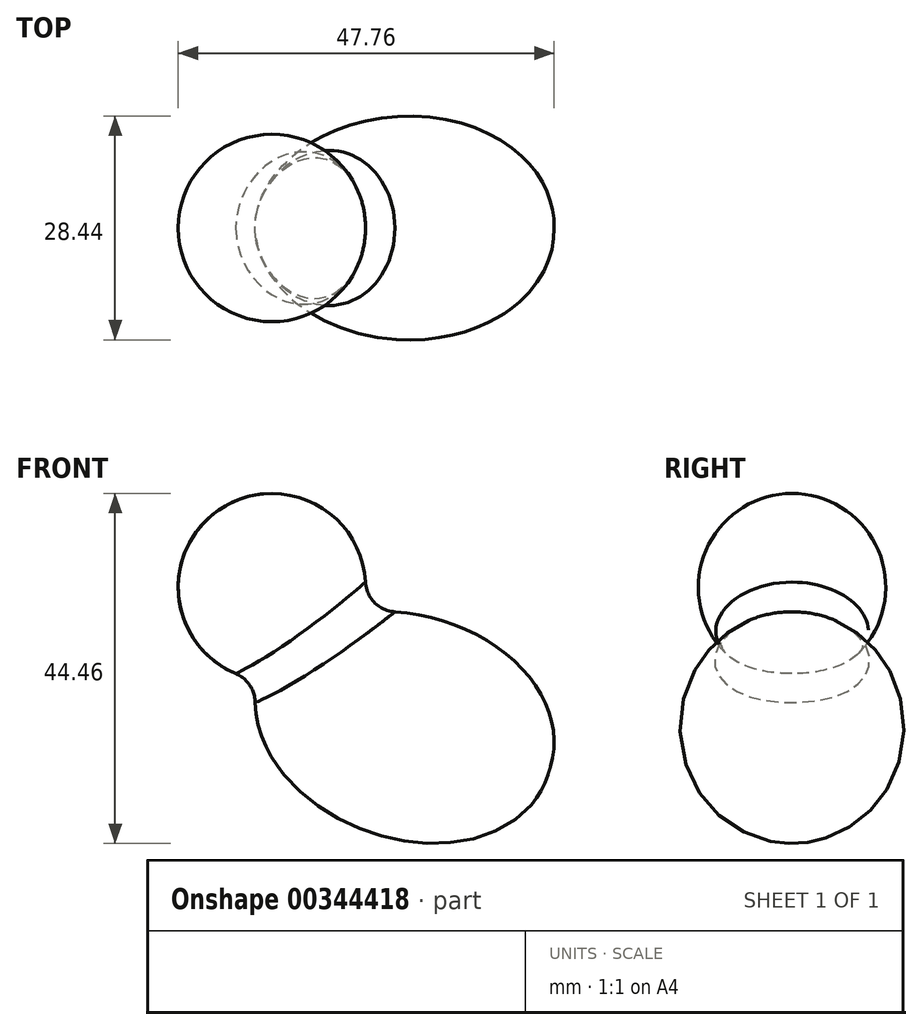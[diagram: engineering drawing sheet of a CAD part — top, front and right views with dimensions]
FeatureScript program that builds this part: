
annotation { "Feature Type Name" : "Feature", "Feature Type Description" : "" }
export const myFeature = defineFeature(function(context is Context, id is Id, definition is map)
    precondition{}
    {
        {
            var Q0;
            Q0=qCreatedBy(makeId("Front.planeOp"),FACE);
            var sketch = newSketch(context, id + "F0", { "sketchPlane" : qUnion([Q0])});
            skEllipticalArc(sketch, "E0", {});
            skArc(sketch, "E1", {"start": v(-6.04, -4.15) * mm, "mid": v(7.6, 6.73) * mm, "end": v(-4.26, 19.53) * mm});
            skLineSegment(sketch, "E2", {"start": v(-4.26, 7.62) * mm, "end": v(-4.26, 49.35) * mm});
            skLineSegment(sketch, "E3", {"start": v(12.43, -9.98) * mm, "end": v(15.75, 3.82) * mm});
            skLineSegment(sketch, "E4", {"start": v(12.43, -9.98) * mm, "end": v(-6.09, -4.27) * mm});
            skLineSegment(sketch, "E5", {"start": v(12.43, -9.98) * mm, "end": v(30.95, -15.69) * mm});
            skLineSegment(sketch, "E6", {"start": v(-4.26, 7.62) * mm, "end": v(-4.26, -4.28) * mm});
            const initialGuessF0  = {"E0": [0.012429436668753624, -0.00997983943670988, 0.9723023674645033, -0.23372656293823788, 0.019408537035855263, 0.014195, 6.19712130028944, 3.055528646699647]};
            skSetInitialGuess(sketch, initialGuessF0);
            skSolve(sketch);
        }
        {
            var Q0;
            {var subQ0=sQuery(id+"F0.wireOp",EDGE,"E1");var subQ1=sQuery(id+"F0.wireOp",EDGE,"E0");var subQ2=makeQuery(id+"F0.imprint","INTERSECT",VERTEX,{"disambiguationData":[OD(0.0)],"derivedFrom":[subQ1,subQ0]});Q0=makeQuery(id+"F0.imprint","IMPRINT",FACE,{"disambiguationData":[TD([[makeQuery(id+"F0.imprint","IMPRINT",EDGE,{"disambiguationData":[TD([[subQ2,1.0]])],"derivedFrom":subQ1}),1.0]])]});}
            var Q1;
            {var subQ0=sQuery(id+"F0.wireOp",EDGE,"E3");Q1=makeQuery(id+"F0.imprint","IMPRINT",FACE,{"disambiguationData":[TD([[makeQuery(id+"F0.imprint","IMPRINT",EDGE,{"derivedFrom":subQ0}),-1.0]])]});}
            var Q2;
            {var subQ6=sQuery(id+"F0.wireOp",EDGE,"E3");Q2=makeQuery(id+"F0.imprint","IMPRINT",FACE,{"disambiguationData":[TD([[makeQuery(id+"F0.imprint","IMPRINT",EDGE,{"derivedFrom":subQ6}),1.0]])]});}
            var Q3;
            {var subQ0=sQuery(id+"F0.wireOp",EDGE,"E1");var subQ1=sQuery(id+"F0.wireOp",EDGE,"E0");var subQ2=makeQuery(id+"F0.imprint","INTERSECT",VERTEX,{"disambiguationData":[OD(1.0)],"derivedFrom":[subQ1,subQ0]});Q3=makeQuery(id+"F0.imprint","IMPRINT",FACE,{"disambiguationData":[TD([[makeQuery(id+"F0.imprint","IMPRINT",EDGE,{"disambiguationData":[TD([[subQ2,-1.0]])],"derivedFrom":subQ1}),1.0]])]});}
            var Q4;
            Q4=sQuery(id+"F0.wireOp",EDGE,"E4");
            revolve(context, id + "F1", {"entities" : qUnion([Q0, Q1, Q2, Q3]), "axis" : qUnion([Q4]), "revolveType" : RevolveType.FULL});
        }
        {
            var Q0;
            Q0=qCreatedBy(makeId("Front.planeOp"),FACE);
            var sketch = newSketch(context, id + "F2", { "sketchPlane" : qUnion([Q0])});
            skArc(sketch, "E7.0", {"start": v(-4.26, -4.28) * mm, "mid": v(7.64, 7.62) * mm, "end": v(-4.26, 19.53) * mm});
            skLineSegment(sketch, "E7.1", {"start": v(-4.26, 7.62) * mm, "end": v(-4.26, -4.28) * mm});
            skLineSegment(sketch, "E7.2", {"start": v(-4.26, 7.62) * mm, "end": v(-4.26, 19.53) * mm});
            skPoint(sketch, "E8.orphan", {"position": v(-4.26, 49.35) * mm});
            skPoint(sketch, "E9.orphan", {"position": v(-6.04, -4.15) * mm});
            skSolve(sketch);
        }
        {
            var Q0;
            Q0 = qSketchRegion(id + "F2", true);
            var Q1;
            Q1=sQuery(id+"F2.wireOp",EDGE,"E7.2");
            revolve(context, id + "F3", {"operationType" : NewBodyOperationType.ADD, "entities" : qUnion([Q0]), "axis" : qUnion([Q1]), "revolveType" : RevolveType.FULL});
        }
        {
            var Q0;
            Q0=makeQuery(id+"F3.boolean.opBoolean","INTERSECT",EDGE,{"derivedFrom":[makeQuery(id+"F1.opRevolve","SWEPT_FACE",FACE,{"disambiguationData":[OSD([sQuery(id+"F0.wireOp",EDGE,"E0")])]}),makeQuery(id+"F3.opRevolve","SWEPT_FACE",FACE,{"disambiguationData":[OSD([sQuery(id+"F2.wireOp",EDGE,"E7.0")])]})]});
            fillet(context, id + "F4", {"entities" : qUnion([Q0]), "radius" : 4 * mm, "tangentPropagation" : true, "allowEdgeOverflow" : false});
        }
    });
